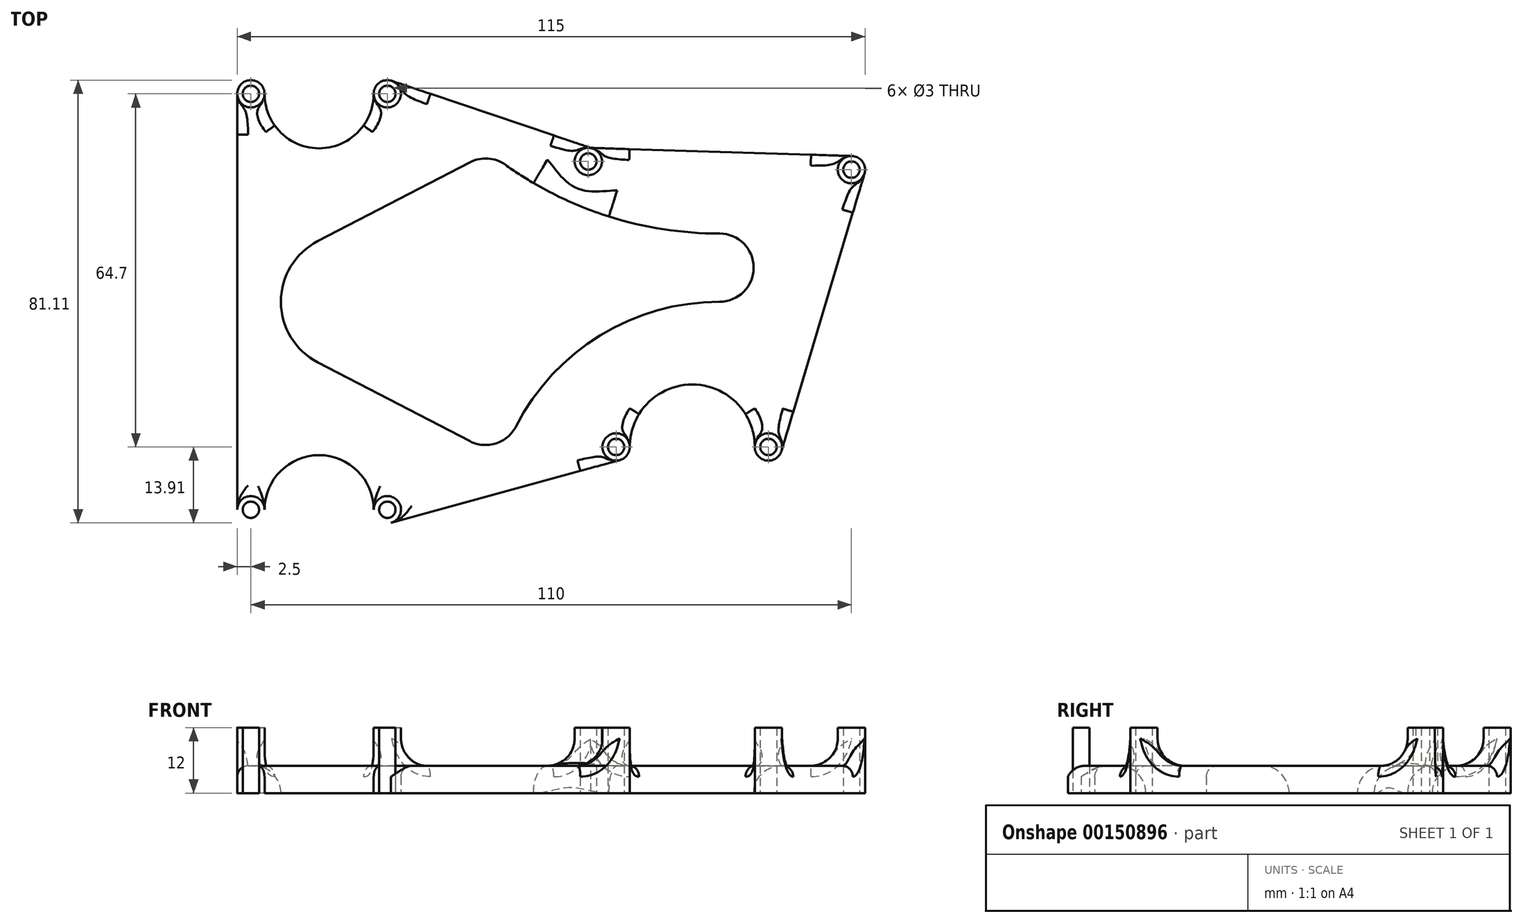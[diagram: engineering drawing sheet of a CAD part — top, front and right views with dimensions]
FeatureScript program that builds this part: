
annotation { "Feature Type Name" : "Feature", "Feature Type Description" : "" }
export const myFeature = defineFeature(function(context is Context, id is Id, definition is map)
    precondition{}
    {
        {
            var Q0;
            Q0=qCreatedBy(makeId("Top.planeOp"),FACE);
            var sketch = newSketch(context, id + "F0", { "sketchPlane" : qUnion([Q0])});
            skLineSegment(sketch, "E0.bottom", {"start": v(-142, 86) * mm, "end": v(0, 86) * mm, "construction": true});
            skLineSegment(sketch, "E0.top", {"start": v(-142, 0) * mm, "end": v(0, 0) * mm, "construction": true});
            skLineSegment(sketch, "E0.left", {"start": v(-142, 86) * mm, "end": v(-142, 0) * mm, "construction": true});
            skLineSegment(sketch, "E0.right", {"start": v(0, 86) * mm, "end": v(0, 0) * mm, "construction": true});
            skLineSegment(sketch, "E1", {"start": v(-57, 86) * mm, "end": v(-57, 0) * mm, "construction": true});
            skLineSegment(sketch, "E2", {"start": v(-53.3, 86) * mm, "end": v(-53.3, 0) * mm, "construction": true});
            skCircle(sketch, "E3", {"center": v(-112.6, 81.1) * mm, "radius": 1.5 * mm});
            skCircle(sketch, "E4", {"center": v(-87.6, 81.1) * mm, "radius": 1.5 * mm});
            skLineSegment(sketch, "E5", {"start": v(-142, 43) * mm, "end": v(0, 43) * mm, "construction": true});
            skCircle(sketch, "E6.MirrorC", {"center": v(-87.6, 4.9) * mm, "radius": 1.5 * mm});
            skCircle(sketch, "E7.MirrorC", {"center": v(-112.6, 4.9) * mm, "radius": 1.5 * mm});
            skCircle(sketch, "E8", {"center": v(-50.8, 68.7) * mm, "radius": 1.5 * mm});
            skCircle(sketch, "E9", {"center": v(-2.6, 67.2) * mm, "radius": 1.5 * mm});
            skCircle(sketch, "E10", {"center": v(-17.8, 16.4) * mm, "radius": 1.5 * mm});
            skCircle(sketch, "E11", {"center": v(-45.7, 16.4) * mm, "radius": 1.5 * mm});
            skLineSegment(sketch, "E12", {"start": v(0, 68.7) * mm, "end": v(-53.3, 68.7) * mm, "construction": true});
            skCircle(sketch, "E13", {"center": v(-112.6, 81.1) * mm, "radius": 2.5 * mm});
            skCircle(sketch, "E14", {"center": v(-87.6, 81.1) * mm, "radius": 2.5 * mm});
            skCircle(sketch, "E15", {"center": v(-112.6, 4.9) * mm, "radius": 2.5 * mm});
            skCircle(sketch, "E16", {"center": v(-87.6, 4.9) * mm, "radius": 2.5 * mm});
            skCircle(sketch, "E17", {"center": v(-45.7, 16.4) * mm, "radius": 2.5 * mm});
            skCircle(sketch, "E18", {"center": v(-17.8, 16.4) * mm, "radius": 2.5 * mm});
            skCircle(sketch, "E19", {"center": v(-50.8, 68.7) * mm, "radius": 2.5 * mm});
            skCircle(sketch, "E20", {"center": v(-2.6, 67.2) * mm, "radius": 2.5 * mm});
            skLineSegment(sketch, "E21", {"start": v(-115.1, 81.1) * mm, "end": v(-115.1, 4.9) * mm});
            skArc(sketch, "E22", {"start": v(-90.1, 4.9) * mm, "mid": v(-100.1, 14.9) * mm, "end": v(-110.1, 4.9) * mm});
            skArc(sketch, "E23.MirrorCS", {"start": v(-90.1, 81.1) * mm, "mid": v(-100.1, 71.1) * mm, "end": v(-110.1, 81.1) * mm});
            skLineSegment(sketch, "E24", {"start": v(-86.94, 2.49) * mm, "end": v(-45.04, 13.99) * mm});
            skLineSegment(sketch, "E25", {"start": v(-86.8, 83.47) * mm, "end": v(-50, 71.07) * mm});
            skLineSegment(sketch, "E26", {"start": v(-50.72, 71.2) * mm, "end": v(-2.52, 69.7) * mm});
            skLineSegment(sketch, "E27", {"start": v(-15.4, 15.68) * mm, "end": v(-0.2, 66.48) * mm});
            skArc(sketch, "E28", {"start": v(-20.3, 16.4) * mm, "mid": v(-31.75, 27.85) * mm, "end": v(-43.2, 16.4) * mm});
            skLineSegment(sketch, "E29", {"start": v(-100.35, 54.1) * mm, "end": v(-72.48, 68.55) * mm});
            skLineSegment(sketch, "E30", {"start": v(-100.35, 31.9) * mm, "end": v(-72.48, 17.45) * mm});
            skLineSegment(sketch, "E31", {"start": v(-69.6, 63) * mm, "end": v(-69.6, 23) * mm, "construction": true});
            skArc(sketch, "E32", {"start": v(-26.76, 43) * mm, "mid": v(-48.62, 36.84) * mm, "end": v(-64.03, 20.16) * mm});
            skArc(sketch, "E33", {"start": v(-65.96, 68.08) * mm, "mid": v(-47.35, 58.72) * mm, "end": v(-26.76, 55.5) * mm});
            skArc(sketch, "E34", {"start": v(-100.35, 54.1) * mm, "mid": v(-107.1, 43) * mm, "end": v(-100.35, 31.9) * mm});
            skArc(sketch, "E35", {"start": v(-100.35, 31.9) * mm, "mid": v(-82.1, 43) * mm, "end": v(-100.35, 54.1) * mm, "construction": true});
            skArc(sketch, "E36", {"start": v(-72.48, 17.45) * mm, "mid": v(-67.69, 17.05) * mm, "end": v(-64.03, 20.16) * mm});
            skArc(sketch, "E37", {"start": v(-64.03, 20.16) * mm, "mid": v(-71.51, 28.95) * mm, "end": v(-72.48, 17.45) * mm, "construction": true});
            skArc(sketch, "E38", {"start": v(-26.76, 43) * mm, "mid": v(-20.5, 49.25) * mm, "end": v(-26.76, 55.5) * mm});
            skArc(sketch, "E39", {"start": v(-26.76, 55.5) * mm, "mid": v(-33, 49.25) * mm, "end": v(-26.76, 43) * mm, "construction": true});
            skArc(sketch, "E40", {"start": v(-65.96, 68.08) * mm, "mid": v(-69.15, 69.23) * mm, "end": v(-72.48, 68.55) * mm});
            skArc(sketch, "E41", {"start": v(-72.48, 68.55) * mm, "mid": v(-70.05, 56.77) * mm, "end": v(-65.96, 68.08) * mm, "construction": true});
            skSolve(sketch);
        }
        {
            var Q0;
            {var subQ17=sQuery(id+"F0.wireOp",EDGE,"E21");Q0=makeQuery(id+"F0.imprint","IMPRINT",FACE,{"disambiguationData":[TD([[makeQuery(id+"F0.imprint","IMPRINT",EDGE,{"derivedFrom":subQ17}),1.0]])]});}
            var Q1;
            Q1=makeQuery(id+"F0.imprint","IMPRINT",FACE,{"disambiguationData":[TD([[makeQuery(id+"F0.imprint","IMPRINT",EDGE,{"derivedFrom":sQuery(id+"F0.wireOp",EDGE,"E11")}),-1.0]])]});
            var Q2;
            Q2=makeQuery(id+"F0.imprint","IMPRINT",FACE,{"disambiguationData":[TD([[makeQuery(id+"F0.imprint","IMPRINT",EDGE,{"derivedFrom":sQuery(id+"F0.wireOp",EDGE,"E9")}),-1.0]])]});
            var Q3;
            Q3=makeQuery(id+"F0.imprint","IMPRINT",FACE,{"disambiguationData":[TD([[makeQuery(id+"F0.imprint","IMPRINT",EDGE,{"derivedFrom":sQuery(id+"F0.wireOp",EDGE,"E7.MirrorC")}),1.0]])]});
            var Q4;
            Q4=makeQuery(id+"F0.imprint","IMPRINT",FACE,{"disambiguationData":[TD([[makeQuery(id+"F0.imprint","IMPRINT",EDGE,{"derivedFrom":sQuery(id+"F0.wireOp",EDGE,"E8")}),-1.0]])]});
            var Q5;
            Q5=makeQuery(id+"F0.imprint","IMPRINT",FACE,{"disambiguationData":[TD([[makeQuery(id+"F0.imprint","IMPRINT",EDGE,{"derivedFrom":sQuery(id+"F0.wireOp",EDGE,"E6.MirrorC")}),1.0]])]});
            var Q6;
            Q6=makeQuery(id+"F0.imprint","IMPRINT",FACE,{"disambiguationData":[TD([[makeQuery(id+"F0.imprint","IMPRINT",EDGE,{"derivedFrom":sQuery(id+"F0.wireOp",EDGE,"E4")}),-1.0]])]});
            var Q7;
            {var subQ0=sQuery(id+"F0.wireOp",EDGE,"E25");var subQ1=sQuery(id+"F0.wireOp",EDGE,"E19");var subQ2=makeQuery(id+"F0.imprint","INTERSECT",VERTEX,{"derivedFrom":[subQ1,subQ0]});Q7=makeQuery(id+"F0.imprint","IMPRINT",FACE,{"disambiguationData":[TD([[makeQuery(id+"F0.imprint","IMPRINT",EDGE,{"disambiguationData":[TD([[subQ2,-1.0]])],"derivedFrom":subQ1}),-1.0]])]});}
            var Q8;
            Q8=makeQuery(id+"F0.imprint","IMPRINT",FACE,{"disambiguationData":[TD([[makeQuery(id+"F0.imprint","IMPRINT",EDGE,{"derivedFrom":sQuery(id+"F0.wireOp",EDGE,"E3")}),-1.0]])]});
            var Q9;
            Q9=makeQuery(id+"F0.imprint","IMPRINT",FACE,{"disambiguationData":[TD([[makeQuery(id+"F0.imprint","IMPRINT",EDGE,{"derivedFrom":sQuery(id+"F0.wireOp",EDGE,"E10")}),-1.0]])]});
            extrude(context, id + "F1", {"entities" : qUnion([Q0, Q1, Q2, Q3, Q4, Q5, Q6, Q7, Q8, Q9]), "depth" : 5 * mm});
        }
        {
            var Q0;
            Q0=makeQuery(id+"F0.imprint","IMPRINT",FACE,{"disambiguationData":[TD([[makeQuery(id+"F0.imprint","IMPRINT",EDGE,{"derivedFrom":sQuery(id+"F0.wireOp",EDGE,"E7.MirrorC")}),1.0]])]});
            var Q1;
            Q1=makeQuery(id+"F0.imprint","IMPRINT",FACE,{"disambiguationData":[TD([[makeQuery(id+"F0.imprint","IMPRINT",EDGE,{"derivedFrom":sQuery(id+"F0.wireOp",EDGE,"E6.MirrorC")}),1.0]])]});
            var Q2;
            Q2=makeQuery(id+"F0.imprint","IMPRINT",FACE,{"disambiguationData":[TD([[makeQuery(id+"F0.imprint","IMPRINT",EDGE,{"derivedFrom":sQuery(id+"F0.wireOp",EDGE,"E3")}),-1.0]])]});
            var Q3;
            Q3=makeQuery(id+"F0.imprint","IMPRINT",FACE,{"disambiguationData":[TD([[makeQuery(id+"F0.imprint","IMPRINT",EDGE,{"derivedFrom":sQuery(id+"F0.wireOp",EDGE,"E4")}),-1.0]])]});
            var Q4;
            Q4=makeQuery(id+"F0.imprint","IMPRINT",FACE,{"disambiguationData":[TD([[makeQuery(id+"F0.imprint","IMPRINT",EDGE,{"derivedFrom":sQuery(id+"F0.wireOp",EDGE,"E8")}),-1.0]])]});
            var Q5;
            Q5=makeQuery(id+"F0.imprint","IMPRINT",FACE,{"disambiguationData":[TD([[makeQuery(id+"F0.imprint","IMPRINT",EDGE,{"derivedFrom":sQuery(id+"F0.wireOp",EDGE,"E9")}),-1.0]])]});
            var Q6;
            Q6=makeQuery(id+"F0.imprint","IMPRINT",FACE,{"disambiguationData":[TD([[makeQuery(id+"F0.imprint","IMPRINT",EDGE,{"derivedFrom":sQuery(id+"F0.wireOp",EDGE,"E10")}),-1.0]])]});
            var Q7;
            Q7=makeQuery(id+"F0.imprint","IMPRINT",FACE,{"disambiguationData":[TD([[makeQuery(id+"F0.imprint","IMPRINT",EDGE,{"derivedFrom":sQuery(id+"F0.wireOp",EDGE,"E11")}),-1.0]])]});
            extrude(context, id + "F2", {"entities" : qUnion([Q0, Q1, Q2, Q3, Q4, Q5, Q6, Q7]), "operationType" : NewBodyOperationType.ADD, "depth" : 12 * mm});
        }
        {
            var Q0;
            {var subQ0=sQuery(id+"F0.wireOp",EDGE,"E13");Q0=makeQuery(id+"F2.boolean.opBoolean","INTERSECT",EDGE,{"derivedFrom":[makeQuery(id+"F1.opExtrude","CAP_FACE",FACE,{"disambiguationData":[OSD([sQuery(id+"F0.wireOp",EDGE,"E3"),sQuery(id+"F0.wireOp",EDGE,"E4"),sQuery(id+"F0.wireOp",EDGE,"E6.MirrorC"),sQuery(id+"F0.wireOp",EDGE,"E7.MirrorC"),sQuery(id+"F0.wireOp",EDGE,"E8"),sQuery(id+"F0.wireOp",EDGE,"E9"),sQuery(id+"F0.wireOp",EDGE,"E10"),sQuery(id+"F0.wireOp",EDGE,"E11"),subQ0,sQuery(id+"F0.wireOp",EDGE,"E14"),sQuery(id+"F0.wireOp",EDGE,"E15"),sQuery(id+"F0.wireOp",EDGE,"E16"),sQuery(id+"F0.wireOp",EDGE,"E17"),sQuery(id+"F0.wireOp",EDGE,"E18"),sQuery(id+"F0.wireOp",EDGE,"E20"),sQuery(id+"F0.wireOp",EDGE,"E21"),sQuery(id+"F0.wireOp",EDGE,"E22"),sQuery(id+"F0.wireOp",EDGE,"E23.MirrorCS"),sQuery(id+"F0.wireOp",EDGE,"E24"),sQuery(id+"F0.wireOp",EDGE,"E25"),sQuery(id+"F0.wireOp",EDGE,"E26"),sQuery(id+"F0.wireOp",EDGE,"E27"),sQuery(id+"F0.wireOp",EDGE,"E28"),sQuery(id+"F0.wireOp",EDGE,"E29"),sQuery(id+"F0.wireOp",EDGE,"E30"),sQuery(id+"F0.wireOp",EDGE,"E32"),sQuery(id+"F0.wireOp",EDGE,"E33"),sQuery(id+"F0.wireOp",EDGE,"E34"),sQuery(id+"F0.wireOp",EDGE,"E36"),sQuery(id+"F0.wireOp",EDGE,"E38"),sQuery(id+"F0.wireOp",EDGE,"E40")])],"isStart":false}),makeQuery(id+"F2.opExtrude","SWEPT_FACE",FACE,{"disambiguationData":[OSD([subQ0])]})]});}
            var Q1;
            {var subQ0=sQuery(id+"F0.wireOp",EDGE,"E14");Q1=makeQuery(id+"F2.boolean.opBoolean","INTERSECT",EDGE,{"derivedFrom":[makeQuery(id+"F1.opExtrude","CAP_FACE",FACE,{"disambiguationData":[OSD([sQuery(id+"F0.wireOp",EDGE,"E3"),sQuery(id+"F0.wireOp",EDGE,"E4"),sQuery(id+"F0.wireOp",EDGE,"E6.MirrorC"),sQuery(id+"F0.wireOp",EDGE,"E7.MirrorC"),sQuery(id+"F0.wireOp",EDGE,"E8"),sQuery(id+"F0.wireOp",EDGE,"E9"),sQuery(id+"F0.wireOp",EDGE,"E10"),sQuery(id+"F0.wireOp",EDGE,"E11"),sQuery(id+"F0.wireOp",EDGE,"E13"),subQ0,sQuery(id+"F0.wireOp",EDGE,"E15"),sQuery(id+"F0.wireOp",EDGE,"E16"),sQuery(id+"F0.wireOp",EDGE,"E17"),sQuery(id+"F0.wireOp",EDGE,"E18"),sQuery(id+"F0.wireOp",EDGE,"E20"),sQuery(id+"F0.wireOp",EDGE,"E21"),sQuery(id+"F0.wireOp",EDGE,"E22"),sQuery(id+"F0.wireOp",EDGE,"E23.MirrorCS"),sQuery(id+"F0.wireOp",EDGE,"E24"),sQuery(id+"F0.wireOp",EDGE,"E25"),sQuery(id+"F0.wireOp",EDGE,"E26"),sQuery(id+"F0.wireOp",EDGE,"E27"),sQuery(id+"F0.wireOp",EDGE,"E28"),sQuery(id+"F0.wireOp",EDGE,"E29"),sQuery(id+"F0.wireOp",EDGE,"E30"),sQuery(id+"F0.wireOp",EDGE,"E32"),sQuery(id+"F0.wireOp",EDGE,"E33"),sQuery(id+"F0.wireOp",EDGE,"E34"),sQuery(id+"F0.wireOp",EDGE,"E36"),sQuery(id+"F0.wireOp",EDGE,"E38"),sQuery(id+"F0.wireOp",EDGE,"E40")])],"isStart":false}),makeQuery(id+"F2.opExtrude","SWEPT_FACE",FACE,{"disambiguationData":[OSD([subQ0])]})]});}
            var Q2;
            {var subQ0=sQuery(id+"F0.wireOp",EDGE,"E15");Q2=makeQuery(id+"F2.boolean.opBoolean","INTERSECT",EDGE,{"derivedFrom":[makeQuery(id+"F1.opExtrude","CAP_FACE",FACE,{"disambiguationData":[OSD([sQuery(id+"F0.wireOp",EDGE,"E3"),sQuery(id+"F0.wireOp",EDGE,"E4"),sQuery(id+"F0.wireOp",EDGE,"E6.MirrorC"),sQuery(id+"F0.wireOp",EDGE,"E7.MirrorC"),sQuery(id+"F0.wireOp",EDGE,"E8"),sQuery(id+"F0.wireOp",EDGE,"E9"),sQuery(id+"F0.wireOp",EDGE,"E10"),sQuery(id+"F0.wireOp",EDGE,"E11"),sQuery(id+"F0.wireOp",EDGE,"E13"),sQuery(id+"F0.wireOp",EDGE,"E14"),subQ0,sQuery(id+"F0.wireOp",EDGE,"E16"),sQuery(id+"F0.wireOp",EDGE,"E17"),sQuery(id+"F0.wireOp",EDGE,"E18"),sQuery(id+"F0.wireOp",EDGE,"E20"),sQuery(id+"F0.wireOp",EDGE,"E21"),sQuery(id+"F0.wireOp",EDGE,"E22"),sQuery(id+"F0.wireOp",EDGE,"E23.MirrorCS"),sQuery(id+"F0.wireOp",EDGE,"E24"),sQuery(id+"F0.wireOp",EDGE,"E25"),sQuery(id+"F0.wireOp",EDGE,"E26"),sQuery(id+"F0.wireOp",EDGE,"E27"),sQuery(id+"F0.wireOp",EDGE,"E28"),sQuery(id+"F0.wireOp",EDGE,"E29"),sQuery(id+"F0.wireOp",EDGE,"E30"),sQuery(id+"F0.wireOp",EDGE,"E32"),sQuery(id+"F0.wireOp",EDGE,"E33"),sQuery(id+"F0.wireOp",EDGE,"E34"),sQuery(id+"F0.wireOp",EDGE,"E36"),sQuery(id+"F0.wireOp",EDGE,"E38"),sQuery(id+"F0.wireOp",EDGE,"E40")])],"isStart":false}),makeQuery(id+"F2.opExtrude","SWEPT_FACE",FACE,{"disambiguationData":[OSD([subQ0])]})]});}
            var Q3;
            {var subQ0=sQuery(id+"F0.wireOp",EDGE,"E16");Q3=makeQuery(id+"F2.boolean.opBoolean","INTERSECT",EDGE,{"derivedFrom":[makeQuery(id+"F1.opExtrude","CAP_FACE",FACE,{"disambiguationData":[OSD([sQuery(id+"F0.wireOp",EDGE,"E3"),sQuery(id+"F0.wireOp",EDGE,"E4"),sQuery(id+"F0.wireOp",EDGE,"E6.MirrorC"),sQuery(id+"F0.wireOp",EDGE,"E7.MirrorC"),sQuery(id+"F0.wireOp",EDGE,"E8"),sQuery(id+"F0.wireOp",EDGE,"E9"),sQuery(id+"F0.wireOp",EDGE,"E10"),sQuery(id+"F0.wireOp",EDGE,"E11"),sQuery(id+"F0.wireOp",EDGE,"E13"),sQuery(id+"F0.wireOp",EDGE,"E14"),sQuery(id+"F0.wireOp",EDGE,"E15"),subQ0,sQuery(id+"F0.wireOp",EDGE,"E17"),sQuery(id+"F0.wireOp",EDGE,"E18"),sQuery(id+"F0.wireOp",EDGE,"E20"),sQuery(id+"F0.wireOp",EDGE,"E21"),sQuery(id+"F0.wireOp",EDGE,"E22"),sQuery(id+"F0.wireOp",EDGE,"E23.MirrorCS"),sQuery(id+"F0.wireOp",EDGE,"E24"),sQuery(id+"F0.wireOp",EDGE,"E25"),sQuery(id+"F0.wireOp",EDGE,"E26"),sQuery(id+"F0.wireOp",EDGE,"E27"),sQuery(id+"F0.wireOp",EDGE,"E28"),sQuery(id+"F0.wireOp",EDGE,"E29"),sQuery(id+"F0.wireOp",EDGE,"E30"),sQuery(id+"F0.wireOp",EDGE,"E32"),sQuery(id+"F0.wireOp",EDGE,"E33"),sQuery(id+"F0.wireOp",EDGE,"E34"),sQuery(id+"F0.wireOp",EDGE,"E36"),sQuery(id+"F0.wireOp",EDGE,"E38"),sQuery(id+"F0.wireOp",EDGE,"E40")])],"isStart":false}),makeQuery(id+"F2.opExtrude","SWEPT_FACE",FACE,{"disambiguationData":[OSD([subQ0])]})]});}
            var Q4;
            {var subQ0=sQuery(id+"F0.wireOp",EDGE,"E17");Q4=makeQuery(id+"F2.boolean.opBoolean","INTERSECT",EDGE,{"derivedFrom":[makeQuery(id+"F1.opExtrude","CAP_FACE",FACE,{"disambiguationData":[OSD([sQuery(id+"F0.wireOp",EDGE,"E3"),sQuery(id+"F0.wireOp",EDGE,"E4"),sQuery(id+"F0.wireOp",EDGE,"E6.MirrorC"),sQuery(id+"F0.wireOp",EDGE,"E7.MirrorC"),sQuery(id+"F0.wireOp",EDGE,"E8"),sQuery(id+"F0.wireOp",EDGE,"E9"),sQuery(id+"F0.wireOp",EDGE,"E10"),sQuery(id+"F0.wireOp",EDGE,"E11"),sQuery(id+"F0.wireOp",EDGE,"E13"),sQuery(id+"F0.wireOp",EDGE,"E14"),sQuery(id+"F0.wireOp",EDGE,"E15"),sQuery(id+"F0.wireOp",EDGE,"E16"),subQ0,sQuery(id+"F0.wireOp",EDGE,"E18"),sQuery(id+"F0.wireOp",EDGE,"E20"),sQuery(id+"F0.wireOp",EDGE,"E21"),sQuery(id+"F0.wireOp",EDGE,"E22"),sQuery(id+"F0.wireOp",EDGE,"E23.MirrorCS"),sQuery(id+"F0.wireOp",EDGE,"E24"),sQuery(id+"F0.wireOp",EDGE,"E25"),sQuery(id+"F0.wireOp",EDGE,"E26"),sQuery(id+"F0.wireOp",EDGE,"E27"),sQuery(id+"F0.wireOp",EDGE,"E28"),sQuery(id+"F0.wireOp",EDGE,"E29"),sQuery(id+"F0.wireOp",EDGE,"E30"),sQuery(id+"F0.wireOp",EDGE,"E32"),sQuery(id+"F0.wireOp",EDGE,"E33"),sQuery(id+"F0.wireOp",EDGE,"E34"),sQuery(id+"F0.wireOp",EDGE,"E36"),sQuery(id+"F0.wireOp",EDGE,"E38"),sQuery(id+"F0.wireOp",EDGE,"E40")])],"isStart":false}),makeQuery(id+"F2.opExtrude","SWEPT_FACE",FACE,{"disambiguationData":[OSD([subQ0])]})]});}
            var Q5;
            {var subQ0=sQuery(id+"F0.wireOp",EDGE,"E18");Q5=makeQuery(id+"F2.boolean.opBoolean","INTERSECT",EDGE,{"derivedFrom":[makeQuery(id+"F1.opExtrude","CAP_FACE",FACE,{"disambiguationData":[OSD([sQuery(id+"F0.wireOp",EDGE,"E3"),sQuery(id+"F0.wireOp",EDGE,"E4"),sQuery(id+"F0.wireOp",EDGE,"E6.MirrorC"),sQuery(id+"F0.wireOp",EDGE,"E7.MirrorC"),sQuery(id+"F0.wireOp",EDGE,"E8"),sQuery(id+"F0.wireOp",EDGE,"E9"),sQuery(id+"F0.wireOp",EDGE,"E10"),sQuery(id+"F0.wireOp",EDGE,"E11"),sQuery(id+"F0.wireOp",EDGE,"E13"),sQuery(id+"F0.wireOp",EDGE,"E14"),sQuery(id+"F0.wireOp",EDGE,"E15"),sQuery(id+"F0.wireOp",EDGE,"E16"),sQuery(id+"F0.wireOp",EDGE,"E17"),subQ0,sQuery(id+"F0.wireOp",EDGE,"E20"),sQuery(id+"F0.wireOp",EDGE,"E21"),sQuery(id+"F0.wireOp",EDGE,"E22"),sQuery(id+"F0.wireOp",EDGE,"E23.MirrorCS"),sQuery(id+"F0.wireOp",EDGE,"E24"),sQuery(id+"F0.wireOp",EDGE,"E25"),sQuery(id+"F0.wireOp",EDGE,"E26"),sQuery(id+"F0.wireOp",EDGE,"E27"),sQuery(id+"F0.wireOp",EDGE,"E28"),sQuery(id+"F0.wireOp",EDGE,"E29"),sQuery(id+"F0.wireOp",EDGE,"E30"),sQuery(id+"F0.wireOp",EDGE,"E32"),sQuery(id+"F0.wireOp",EDGE,"E33"),sQuery(id+"F0.wireOp",EDGE,"E34"),sQuery(id+"F0.wireOp",EDGE,"E36"),sQuery(id+"F0.wireOp",EDGE,"E38"),sQuery(id+"F0.wireOp",EDGE,"E40")])],"isStart":false}),makeQuery(id+"F2.opExtrude","SWEPT_FACE",FACE,{"disambiguationData":[OSD([subQ0])]})]});}
            var Q6;
            {var subQ0=sQuery(id+"F0.wireOp",EDGE,"E20");Q6=makeQuery(id+"F2.boolean.opBoolean","INTERSECT",EDGE,{"derivedFrom":[makeQuery(id+"F1.opExtrude","CAP_FACE",FACE,{"disambiguationData":[OSD([sQuery(id+"F0.wireOp",EDGE,"E3"),sQuery(id+"F0.wireOp",EDGE,"E4"),sQuery(id+"F0.wireOp",EDGE,"E6.MirrorC"),sQuery(id+"F0.wireOp",EDGE,"E7.MirrorC"),sQuery(id+"F0.wireOp",EDGE,"E8"),sQuery(id+"F0.wireOp",EDGE,"E9"),sQuery(id+"F0.wireOp",EDGE,"E10"),sQuery(id+"F0.wireOp",EDGE,"E11"),sQuery(id+"F0.wireOp",EDGE,"E13"),sQuery(id+"F0.wireOp",EDGE,"E14"),sQuery(id+"F0.wireOp",EDGE,"E15"),sQuery(id+"F0.wireOp",EDGE,"E16"),sQuery(id+"F0.wireOp",EDGE,"E17"),sQuery(id+"F0.wireOp",EDGE,"E18"),subQ0,sQuery(id+"F0.wireOp",EDGE,"E21"),sQuery(id+"F0.wireOp",EDGE,"E22"),sQuery(id+"F0.wireOp",EDGE,"E23.MirrorCS"),sQuery(id+"F0.wireOp",EDGE,"E24"),sQuery(id+"F0.wireOp",EDGE,"E25"),sQuery(id+"F0.wireOp",EDGE,"E26"),sQuery(id+"F0.wireOp",EDGE,"E27"),sQuery(id+"F0.wireOp",EDGE,"E28"),sQuery(id+"F0.wireOp",EDGE,"E29"),sQuery(id+"F0.wireOp",EDGE,"E30"),sQuery(id+"F0.wireOp",EDGE,"E32"),sQuery(id+"F0.wireOp",EDGE,"E33"),sQuery(id+"F0.wireOp",EDGE,"E34"),sQuery(id+"F0.wireOp",EDGE,"E36"),sQuery(id+"F0.wireOp",EDGE,"E38"),sQuery(id+"F0.wireOp",EDGE,"E40")])],"isStart":false}),makeQuery(id+"F2.opExtrude","SWEPT_FACE",FACE,{"disambiguationData":[OSD([subQ0])]})]});}
            fillet(context, id + "F3", {"entities" : qUnion([Q0, Q1, Q2, Q3, Q4, Q5, Q6]), "radius" : 5 * mm, "tangentPropagation" : true, "allowEdgeOverflow" : false});
        }
        {
            var Q0;
            Q0=makeQuery(id+"F2.boolean.opBoolean","INTERSECT",EDGE,{"derivedFrom":[makeQuery(id+"F1.opExtrude","CAP_FACE",FACE,{"disambiguationData":[OSD([sQuery(id+"F0.wireOp",EDGE,"E3"),sQuery(id+"F0.wireOp",EDGE,"E4"),sQuery(id+"F0.wireOp",EDGE,"E6.MirrorC"),sQuery(id+"F0.wireOp",EDGE,"E7.MirrorC"),sQuery(id+"F0.wireOp",EDGE,"E8"),sQuery(id+"F0.wireOp",EDGE,"E9"),sQuery(id+"F0.wireOp",EDGE,"E10"),sQuery(id+"F0.wireOp",EDGE,"E11"),sQuery(id+"F0.wireOp",EDGE,"E13"),sQuery(id+"F0.wireOp",EDGE,"E14"),sQuery(id+"F0.wireOp",EDGE,"E15"),sQuery(id+"F0.wireOp",EDGE,"E16"),sQuery(id+"F0.wireOp",EDGE,"E17"),sQuery(id+"F0.wireOp",EDGE,"E18"),sQuery(id+"F0.wireOp",EDGE,"E20"),sQuery(id+"F0.wireOp",EDGE,"E21"),sQuery(id+"F0.wireOp",EDGE,"E22"),sQuery(id+"F0.wireOp",EDGE,"E23.MirrorCS"),sQuery(id+"F0.wireOp",EDGE,"E24"),sQuery(id+"F0.wireOp",EDGE,"E25"),sQuery(id+"F0.wireOp",EDGE,"E26"),sQuery(id+"F0.wireOp",EDGE,"E27"),sQuery(id+"F0.wireOp",EDGE,"E28"),sQuery(id+"F0.wireOp",EDGE,"E29"),sQuery(id+"F0.wireOp",EDGE,"E30"),sQuery(id+"F0.wireOp",EDGE,"E32"),sQuery(id+"F0.wireOp",EDGE,"E33"),sQuery(id+"F0.wireOp",EDGE,"E34"),sQuery(id+"F0.wireOp",EDGE,"E36"),sQuery(id+"F0.wireOp",EDGE,"E38"),sQuery(id+"F0.wireOp",EDGE,"E40")])],"isStart":false}),makeQuery(id+"F2.opExtrude","SWEPT_FACE",FACE,{"disambiguationData":[OSD([sQuery(id+"F0.wireOp",EDGE,"E19")])]})]});
            fillet(context, id + "F4", {"entities" : qUnion([Q0]), "radius" : 5 * mm, "tangentPropagation" : true, "allowEdgeOverflow" : false});
        }
        {
            var Q0;
            Q0=makeQuery(id+"F1.opExtrude","CAP_EDGE",EDGE,{"disambiguationData":[OSD([sQuery(id+"F0.wireOp",EDGE,"E29")])],"isStart":false});
            fillet(context, id + "F5", {"entities" : qUnion([Q0]), "radius" : 5 * mm, "tangentPropagation" : true, "allowEdgeOverflow" : false});
        }
        {
            var Q0;
            Q0=makeQuery(id+"F1.opExtrude","CAP_EDGE",EDGE,{"disambiguationData":[OSD([sQuery(id+"F0.wireOp",EDGE,"E21")])],"isStart":false});
            var Q1;
            Q1=makeQuery(id+"F1.opExtrude","CAP_EDGE",EDGE,{"disambiguationData":[OSD([sQuery(id+"F0.wireOp",EDGE,"E23.MirrorCS")])],"isStart":false});
            var Q2;
            Q2=makeQuery(id+"F1.opExtrude","CAP_EDGE",EDGE,{"disambiguationData":[OSD([sQuery(id+"F0.wireOp",EDGE,"E25")])],"isStart":false});
            var Q3;
            Q3=makeQuery(id+"F1.opExtrude","CAP_EDGE",EDGE,{"disambiguationData":[OSD([sQuery(id+"F0.wireOp",EDGE,"E22")])],"isStart":false});
            var Q4;
            Q4=makeQuery(id+"F1.opExtrude","CAP_FACE",FACE,{"disambiguationData":[OSD([sQuery(id+"F0.wireOp",EDGE,"E3"),sQuery(id+"F0.wireOp",EDGE,"E4"),sQuery(id+"F0.wireOp",EDGE,"E6.MirrorC"),sQuery(id+"F0.wireOp",EDGE,"E7.MirrorC"),sQuery(id+"F0.wireOp",EDGE,"E8"),sQuery(id+"F0.wireOp",EDGE,"E9"),sQuery(id+"F0.wireOp",EDGE,"E10"),sQuery(id+"F0.wireOp",EDGE,"E11"),sQuery(id+"F0.wireOp",EDGE,"E13"),sQuery(id+"F0.wireOp",EDGE,"E14"),sQuery(id+"F0.wireOp",EDGE,"E15"),sQuery(id+"F0.wireOp",EDGE,"E16"),sQuery(id+"F0.wireOp",EDGE,"E17"),sQuery(id+"F0.wireOp",EDGE,"E18"),sQuery(id+"F0.wireOp",EDGE,"E20"),sQuery(id+"F0.wireOp",EDGE,"E21"),sQuery(id+"F0.wireOp",EDGE,"E22"),sQuery(id+"F0.wireOp",EDGE,"E23.MirrorCS"),sQuery(id+"F0.wireOp",EDGE,"E24"),sQuery(id+"F0.wireOp",EDGE,"E25"),sQuery(id+"F0.wireOp",EDGE,"E26"),sQuery(id+"F0.wireOp",EDGE,"E27"),sQuery(id+"F0.wireOp",EDGE,"E28"),sQuery(id+"F0.wireOp",EDGE,"E29"),sQuery(id+"F0.wireOp",EDGE,"E30"),sQuery(id+"F0.wireOp",EDGE,"E32"),sQuery(id+"F0.wireOp",EDGE,"E33"),sQuery(id+"F0.wireOp",EDGE,"E34"),sQuery(id+"F0.wireOp",EDGE,"E36"),sQuery(id+"F0.wireOp",EDGE,"E38"),sQuery(id+"F0.wireOp",EDGE,"E40")])],"isStart":false});
            fillet(context, id + "F6", {"entities" : qUnion([Q0, Q1, Q2, Q3, Q4]), "radius" : 2 * mm, "tangentPropagation" : true, "allowEdgeOverflow" : false});
        }
    });
